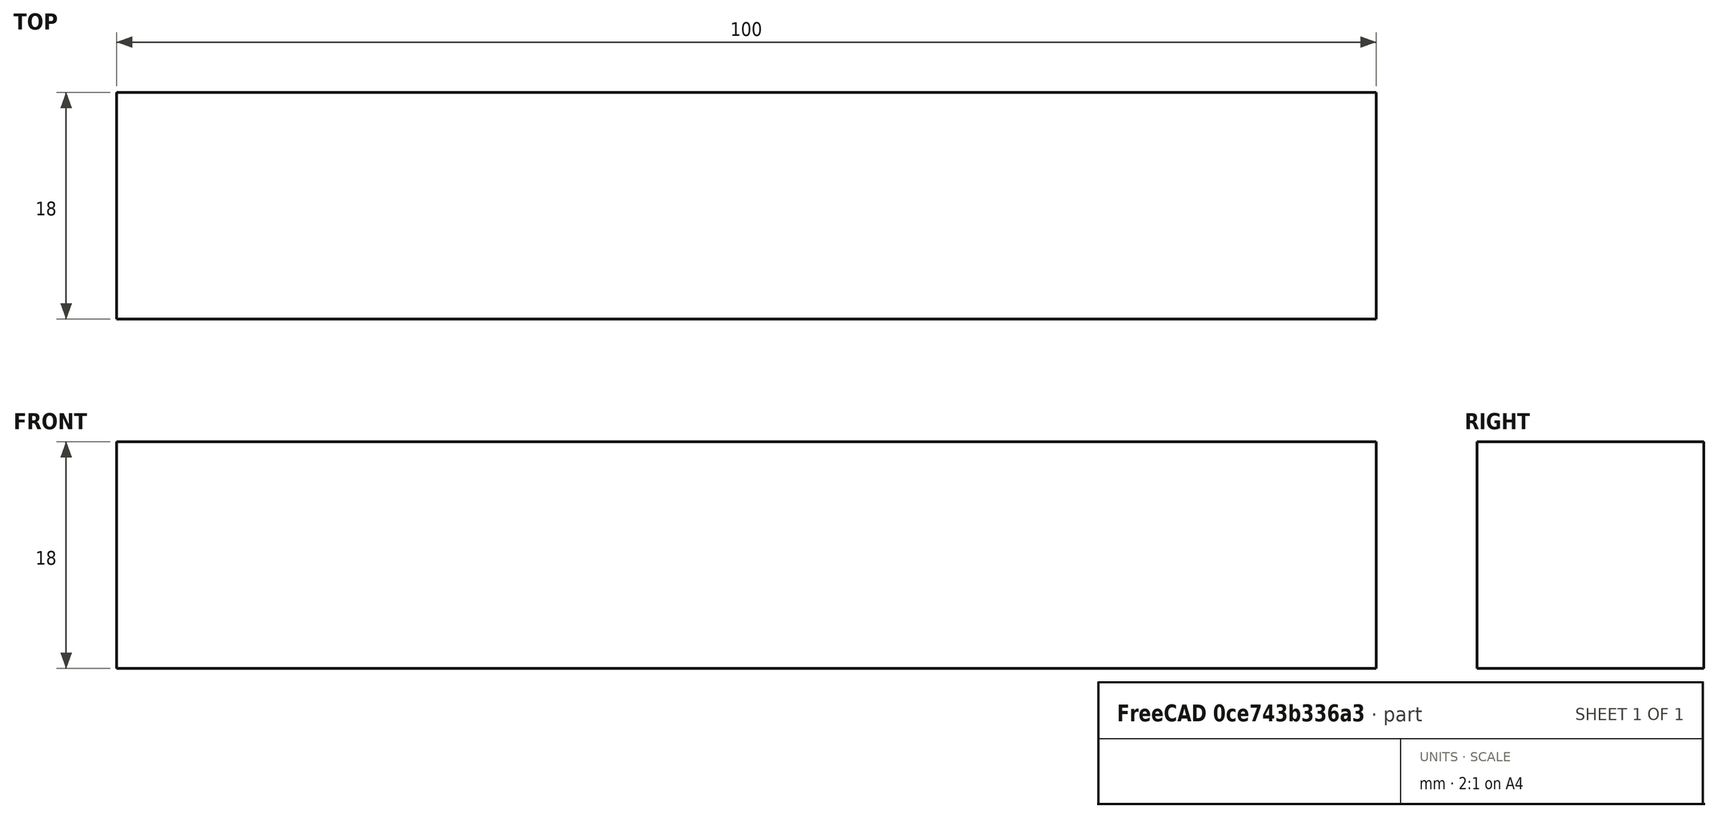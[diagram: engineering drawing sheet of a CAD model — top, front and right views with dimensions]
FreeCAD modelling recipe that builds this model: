
FCSTD DOCUMENT  (FreeCAD 0.19R24291 (Git))
Label: 3000_strut_x_18_18_roof
License: All rights reserved
LicenseURL: http://en.wikipedia.org/wiki/All_rights_reserved
objects: Sketcher::SketchObject×1, PartDesign::Pad×1, PartDesign::Body×1
note: 4 computed .brp shape members not serialized (recipe doc carries the construction recipe); baked Part::Feature solids carry a one-line shape summary decoded from their .brp

FEATURE [Sketcher::SketchObject] Sketch
  FullyConstrained = true
  MapMode = 5
  Placement = pos=(0,0,0) rot=(0.57735,0.57735,0.57735;2.0944rad)
  Support = -> [YZ_Plane]
  sketch-geometry (4):
    g0: LineSegment StartX=0 StartY=18 StartZ=0 EndX=18 EndY=18 EndZ=0
    g1: LineSegment StartX=18 StartY=18 StartZ=0 EndX=18 EndY=0 EndZ=0
    g2: LineSegment StartX=18 StartY=0 StartZ=0 EndX=0 EndY=0 EndZ=0
    g3: LineSegment StartX=0 StartY=0 StartZ=0 EndX=0 EndY=18 EndZ=0
  constraints (12):
    c: Coincident(g0,g1)
    c: Coincident(g1,g2)
    c: Coincident(g2,g3)
    c: Coincident(g3,g0)
    c: Horizontal(g0)
    c: Horizontal(g2)
    c: Vertical(g1)
    c: Vertical(g3)
    c: PointOnObject(g0,g-2)
    c: PointOnObject(g1,g-1)
    c: Equal(g1,g0)
    c: DistanceY(g1,g1) = 18
FEATURE [PartDesign::Pad] Pad
  Direction = (1,1,1)
  Length = 100
  Length2 = 100
  Placement = pos=(0,0,0) rot=(0.57735,0.57735,0.57735;2.0944rad)
  Profile = -> Sketch
  Type = 0
  expr: Length = 100
FEATURE [PartDesign::Body] Body
  Group = -> [Sketch,Pad]
  Origin = -> Origin
  Tip = -> Pad
